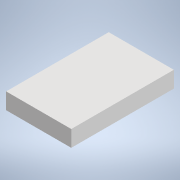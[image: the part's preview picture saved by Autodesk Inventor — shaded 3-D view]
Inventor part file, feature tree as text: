
AUTODESK INVENTOR PART (.ipt)
format: ipt  version: 2021 (Build 250183000, 183)  size: 91,648 bytes
history: native  units: mm
features: extrude x1, sketch x1
ambient origin geometry x8: Origin, YZ Plane, XZ Plane, XY Plane, X Axis, Y Axis, Z Axis, Center Point
bodies: Solid1 (feature_tree)
feature tree (2):
  extrude  "Extrusion1"  Depth=10.0mm
  sketch  "Sketch1"  dims[d0=63.0mm d1=31.5mm d2=40.0mm d3=20.0mm d4=10.0mm d5=0.0mm]
